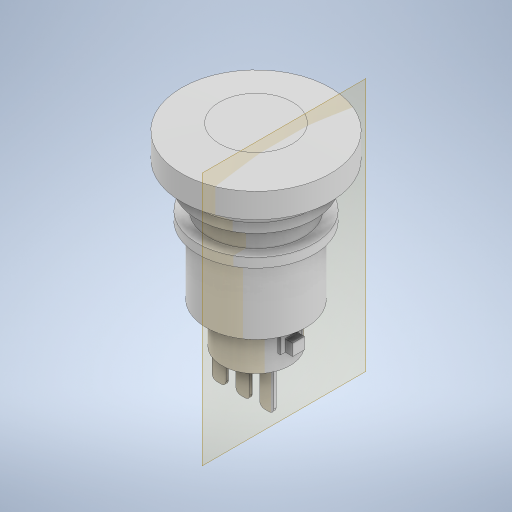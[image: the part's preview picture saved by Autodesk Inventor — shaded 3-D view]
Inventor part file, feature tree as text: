
AUTODESK INVENTOR PART (.ipt)
format: ipt  version: 2024 (Build 280153000, 153)  size: 364,544 bytes
history: native  units: in
note: dims shown in document units (in); Inventor stores cm internally (conversion verified against a paired STEP export)
features: extrude x3, revolve x1, fillet x1, plane x1, sketch x1
ambient origin geometry x8: Origin, YZ Plane, XZ Plane, XY Plane, X Axis, Y Axis, Z Axis, Center Point
bodies: Solid1 (feature_tree)
feature tree (7):
  revolve  "Revolution1"  [1 undecoded]
  extrude  "Extrusion1"  Depth=0.063in
  fillet  "Fillet1"  Radius=0.9783in
  plane  "Work Plane1"
  extrude  "Extrusion2"  Depth=0.063in
  extrude  "Extrusion3"  Depth=0.3425in
  sketch  "Sketch1"  dims[d2=1.252in d3=0.9843in d5=0.7953in d6=0.9783in d9=0.5748in d10=0.3425in d13=0.0787in d14=0.1772in d15=0.1772in d16=0.0787in d17=0.2067in d18=90.0deg d19=0.8386in d20=0.5689in d21=0.6122in d22=0.3248in d23=0.0197in d24=0.1181in d25=0.0827in d26=0.0827in d29=0.5748in d31=0.1102in d32=0.0591in d33=0.315in d34=0.0in d35=0.0394in d36=0.2362in d37=0.1772in d38=0.2165in d39=0.0886in d40=0.0591in d41=0.0in d42=0.0984in d43=0.0984in d44=0.0492in d45=0.063in d46=0.0in]
note: 1 required parameter value undecoded (feature->parameter linkage not recoverable at this tier; creation-order binding heuristic only, values carry confidence <= 0.55)
